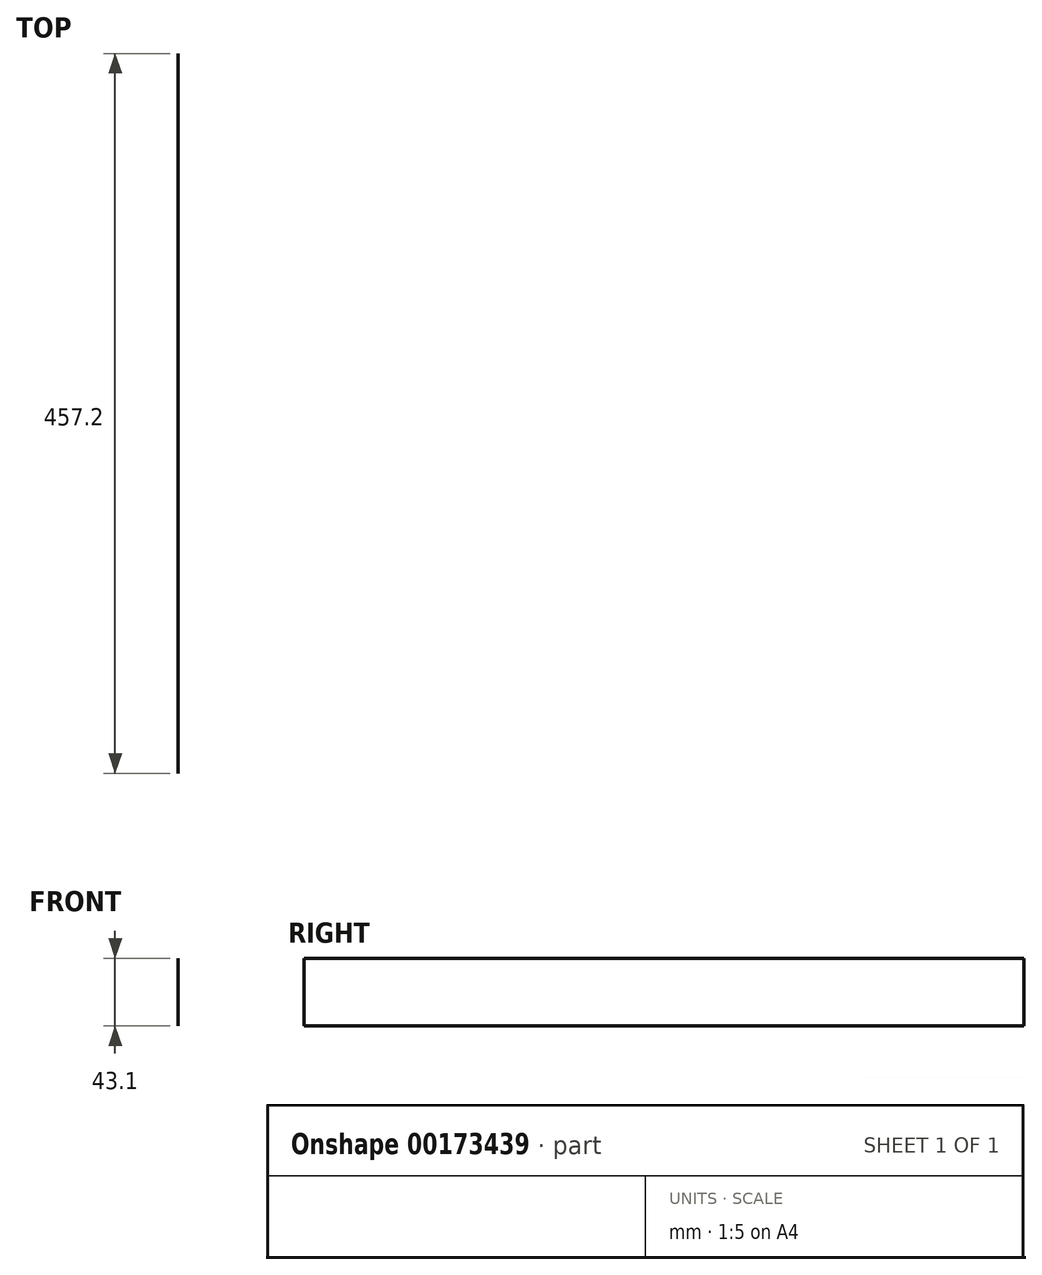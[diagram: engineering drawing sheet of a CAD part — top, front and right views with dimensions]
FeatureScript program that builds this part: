
annotation { "Feature Type Name" : "Feature", "Feature Type Description" : "" }
export const myFeature = defineFeature(function(context is Context, id is Id, definition is map)
    precondition{}
    {
        {
            var Q0;
            Q0=qCreatedBy(makeId("Front.planeOp"),FACE);
            var sketch = newSketch(context, id + "F0", { "sketchPlane" : qUnion([Q0])});
            skLineSegment(sketch, "E0.bottom", {"start": v(0, 21.55) * mm, "end": v(0, 21.55) * mm});
            skLineSegment(sketch, "E0.top", {"start": v(0, -21.55) * mm, "end": v(0, -21.55) * mm});
            skLineSegment(sketch, "E0.left", {"start": v(0, 21.55) * mm, "end": v(0, -21.55) * mm});
            skLineSegment(sketch, "E0.right", {"start": v(0, 21.55) * mm, "end": v(0, -21.55) * mm});
            skPoint(sketch, "E0.middle", {"position": v(0, 0) * mm});
            skSolve(sketch);
        }
        {
            var Q0;
            Q0=sQuery(id+"F0.wireOp",EDGE,"E0.right");
            extrude(context, id + "F1", {"bodyType" : ToolBodyType.SURFACE, "surfaceEntities" : qUnion([Q0]), "depth" : 457.2 * mm});
        }
    });
